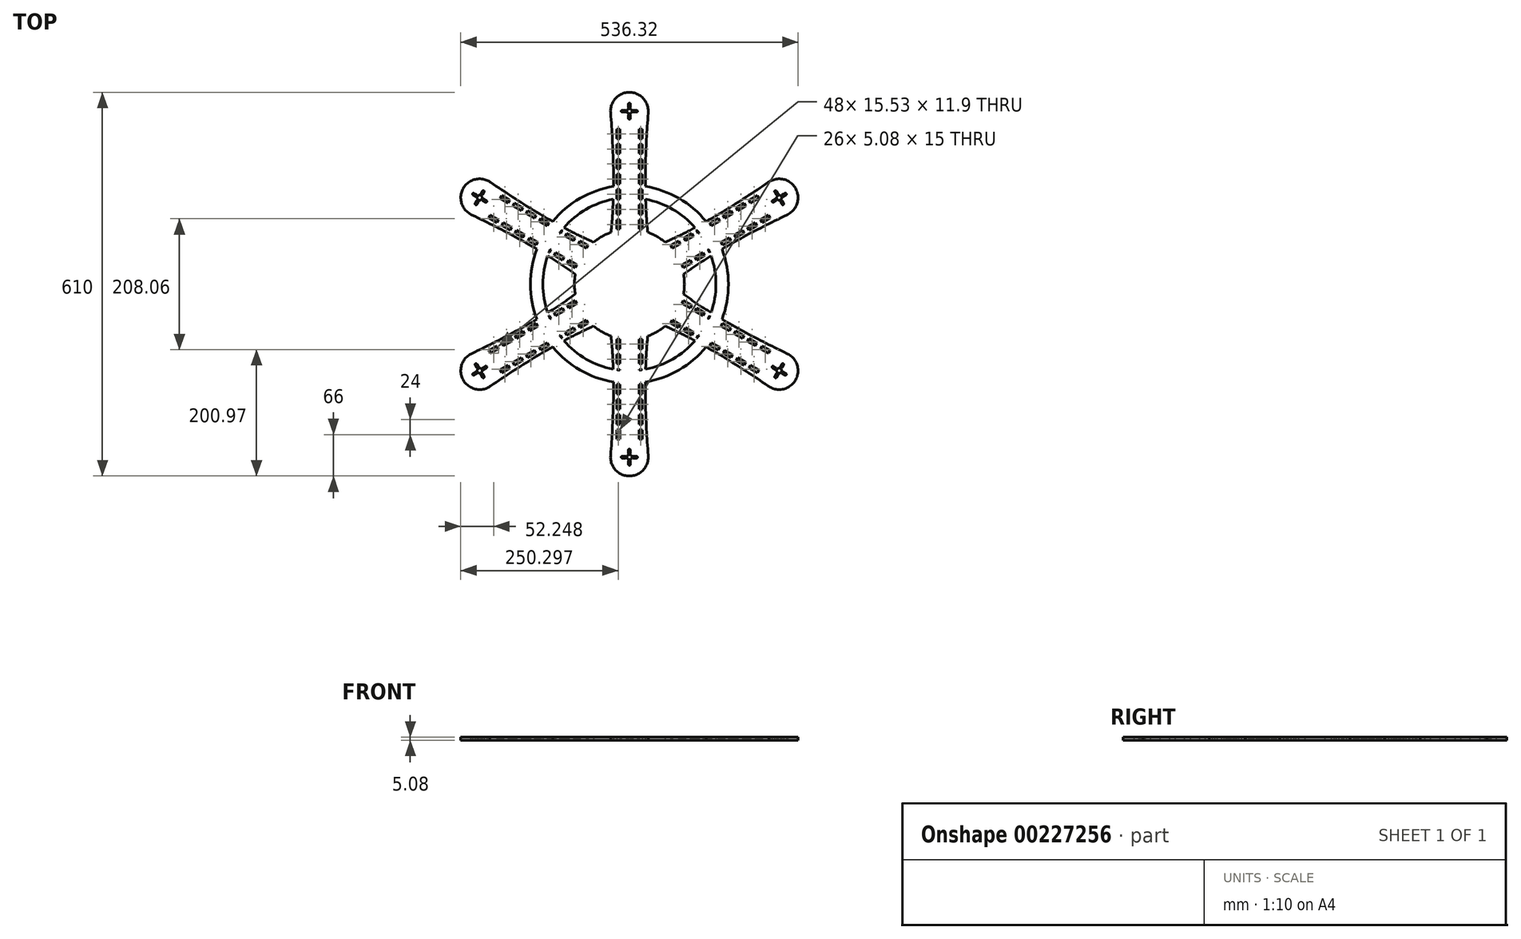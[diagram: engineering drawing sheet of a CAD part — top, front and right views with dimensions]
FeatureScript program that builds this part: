
annotation { "Feature Type Name" : "Feature", "Feature Type Description" : "" }
export const myFeature = defineFeature(function(context is Context, id is Id, definition is map)
    precondition{}
    {
        {
            var Q0;
            Q0=qCreatedBy(makeId("Top.planeOp"),FACE);
            var sketch = newSketch(context, id + "F0", { "sketchPlane" : qUnion([Q0])});
            skCircle(sketch, "E0", {"center": v(0, 0) * mm, "radius": 275 * mm, "construction": true});
            skCircle(sketch, "E1", {"center": v(0, 275) * mm, "radius": 30 * mm});
            skCircle(sketch, "E2", {"center": v(0, 0) * mm, "radius": 87.5 * mm});
            skCircle(sketch, "E3", {"center": v(0, 275) * mm, "radius": 4 * mm});
            skLineSegment(sketch, "E4", {"start": v(0, 275) * mm, "end": v(0, 281.5) * mm, "construction": true});
            skLineSegment(sketch, "E5", {"start": v(0, 281.5) * mm, "end": v(0, 286.5) * mm, "construction": true});
            skCircle(sketch, "E6", {"center": v(0, 286.5) * mm, "radius": 1.5 * mm});
            skCircle(sketch, "E7", {"center": v(0, 281.5) * mm, "radius": 1.5 * mm});
            skLineSegment(sketch, "E8", {"start": v(-1.5, 281.5) * mm, "end": v(-1.5, 286.5) * mm});
            skLineSegment(sketch, "E9.MirrorCS", {"start": v(1.5, 281.5) * mm, "end": v(1.5, 286.5) * mm});
            skLineSegment(sketch, "E10.1.0", {"start": v(-6.5, 276.5) * mm, "end": v(-11.5, 276.5) * mm});
            skCircle(sketch, "E10.1.1", {"center": v(-11.5, 275) * mm, "radius": 1.5 * mm});
            skLineSegment(sketch, "E10.1.2", {"start": v(-6.5, 273.5) * mm, "end": v(-11.5, 273.5) * mm});
            skCircle(sketch, "E10.1.3", {"center": v(-6.5, 275) * mm, "radius": 1.5 * mm});
            skLineSegment(sketch, "E10.2.0", {"start": v(-1.5, 268.5) * mm, "end": v(-1.5, 263.5) * mm});
            skCircle(sketch, "E10.2.1", {"center": v(0, 263.5) * mm, "radius": 1.5 * mm});
            skLineSegment(sketch, "E10.2.2", {"start": v(1.5, 268.5) * mm, "end": v(1.5, 263.5) * mm});
            skCircle(sketch, "E10.2.3", {"center": v(0, 268.5) * mm, "radius": 1.5 * mm});
            skLineSegment(sketch, "E10.3.0", {"start": v(6.5, 273.5) * mm, "end": v(11.5, 273.5) * mm});
            skCircle(sketch, "E10.3.1", {"center": v(11.5, 275) * mm, "radius": 1.5 * mm});
            skLineSegment(sketch, "E10.3.2", {"start": v(6.5, 276.5) * mm, "end": v(11.5, 276.5) * mm});
            skCircle(sketch, "E10.3.3", {"center": v(6.5, 275) * mm, "radius": 1.5 * mm});
            skFitSpline(sketch, "E11", {"points": [v(-29.96, 273.36) * mm, v(-29.27, 82.46) * mm], "startDerivative": vector(15.92, -208.81) * mm, "endDerivative": vector(-18.39, -172.18) * mm});
            skFitSpline(sketch, "E12.MirrorCS", {"points": [v(29.96, 273.36) * mm, v(29.27, 82.46) * mm], "startDerivative": vector(-15.92, -208.81) * mm, "endDerivative": vector(18.39, -172.18) * mm});
            skCircle(sketch, "E13", {"center": v(0, 0) * mm, "radius": 137.5 * mm});
            skCircle(sketch, "E14", {"center": v(0, 0) * mm, "radius": 157.5 * mm});
            skLineSegment(sketch, "E15.bottom", {"start": v(-20.4, 87.5) * mm, "end": v(-15.32, 87.5) * mm});
            skLineSegment(sketch, "E15.top", {"start": v(-20.4, 102.5) * mm, "end": v(-15.32, 102.5) * mm});
            skLineSegment(sketch, "E15.left", {"start": v(-20.4, 87.5) * mm, "end": v(-20.4, 102.5) * mm});
            skLineSegment(sketch, "E15.right", {"start": v(-15.32, 87.5) * mm, "end": v(-15.32, 102.5) * mm});
            skLineSegment(sketch, "E16.MirrorCS", {"start": v(15.32, 87.5) * mm, "end": v(15.32, 102.5) * mm});
            skLineSegment(sketch, "E17.MirrorCS", {"start": v(20.4, 102.5) * mm, "end": v(15.32, 102.5) * mm});
            skLineSegment(sketch, "E18.MirrorCS", {"start": v(20.4, 87.5) * mm, "end": v(20.4, 102.5) * mm});
            skLineSegment(sketch, "E19", {"start": v(15.32, 87.5) * mm, "end": v(20.4, 87.5) * mm});
            skLineSegment(sketch, "E20.0.1.0", {"start": v(-20.4, 111.5) * mm, "end": v(-20.4, 126.5) * mm});
            skLineSegment(sketch, "E20.0.1.1", {"start": v(-20.4, 126.5) * mm, "end": v(-15.32, 126.5) * mm});
            skLineSegment(sketch, "E20.0.1.2", {"start": v(-15.32, 111.5) * mm, "end": v(-15.32, 126.5) * mm});
            skLineSegment(sketch, "E20.0.1.3", {"start": v(-20.4, 111.5) * mm, "end": v(-15.32, 111.5) * mm});
            skLineSegment(sketch, "E20.0.1.4", {"start": v(15.32, 111.5) * mm, "end": v(15.32, 126.5) * mm});
            skLineSegment(sketch, "E20.0.1.5", {"start": v(20.4, 126.5) * mm, "end": v(15.32, 126.5) * mm});
            skLineSegment(sketch, "E20.0.1.6", {"start": v(20.4, 111.5) * mm, "end": v(20.4, 126.5) * mm});
            skLineSegment(sketch, "E20.0.1.7", {"start": v(15.32, 111.5) * mm, "end": v(20.4, 111.5) * mm});
            skLineSegment(sketch, "E20.0.2.0", {"start": v(-20.4, 135.5) * mm, "end": v(-20.4, 150.5) * mm});
            skLineSegment(sketch, "E20.0.2.1", {"start": v(-20.4, 150.5) * mm, "end": v(-15.32, 150.5) * mm});
            skLineSegment(sketch, "E20.0.2.2", {"start": v(-15.32, 135.5) * mm, "end": v(-15.32, 150.5) * mm});
            skLineSegment(sketch, "E20.0.2.3", {"start": v(-20.4, 135.5) * mm, "end": v(-15.32, 135.5) * mm});
            skLineSegment(sketch, "E20.0.2.4", {"start": v(15.32, 135.5) * mm, "end": v(15.32, 150.5) * mm});
            skLineSegment(sketch, "E20.0.2.5", {"start": v(20.4, 150.5) * mm, "end": v(15.32, 150.5) * mm});
            skLineSegment(sketch, "E20.0.2.6", {"start": v(20.4, 135.5) * mm, "end": v(20.4, 150.5) * mm});
            skLineSegment(sketch, "E20.0.2.7", {"start": v(15.32, 135.5) * mm, "end": v(20.4, 135.5) * mm});
            skLineSegment(sketch, "E20.0.3.0", {"start": v(-20.4, 159.5) * mm, "end": v(-20.4, 174.5) * mm});
            skLineSegment(sketch, "E20.0.3.1", {"start": v(-20.4, 174.5) * mm, "end": v(-15.32, 174.5) * mm});
            skLineSegment(sketch, "E20.0.3.2", {"start": v(-15.32, 159.5) * mm, "end": v(-15.32, 174.5) * mm});
            skLineSegment(sketch, "E20.0.3.3", {"start": v(-20.4, 159.5) * mm, "end": v(-15.32, 159.5) * mm});
            skLineSegment(sketch, "E20.0.3.4", {"start": v(15.32, 159.5) * mm, "end": v(15.32, 174.5) * mm});
            skLineSegment(sketch, "E20.0.3.5", {"start": v(20.4, 174.5) * mm, "end": v(15.32, 174.5) * mm});
            skLineSegment(sketch, "E20.0.3.6", {"start": v(20.4, 159.5) * mm, "end": v(20.4, 174.5) * mm});
            skLineSegment(sketch, "E20.0.3.7", {"start": v(15.32, 159.5) * mm, "end": v(20.4, 159.5) * mm});
            skLineSegment(sketch, "E20.0.4.0", {"start": v(-20.4, 183.5) * mm, "end": v(-20.4, 198.5) * mm});
            skLineSegment(sketch, "E20.0.4.1", {"start": v(-20.4, 198.5) * mm, "end": v(-15.32, 198.5) * mm});
            skLineSegment(sketch, "E20.0.4.2", {"start": v(-15.32, 183.5) * mm, "end": v(-15.32, 198.5) * mm});
            skLineSegment(sketch, "E20.0.4.3", {"start": v(-20.4, 183.5) * mm, "end": v(-15.32, 183.5) * mm});
            skLineSegment(sketch, "E20.0.4.4", {"start": v(15.32, 183.5) * mm, "end": v(15.32, 198.5) * mm});
            skLineSegment(sketch, "E20.0.4.5", {"start": v(20.4, 198.5) * mm, "end": v(15.32, 198.5) * mm});
            skLineSegment(sketch, "E20.0.4.6", {"start": v(20.4, 183.5) * mm, "end": v(20.4, 198.5) * mm});
            skLineSegment(sketch, "E20.0.4.7", {"start": v(15.32, 183.5) * mm, "end": v(20.4, 183.5) * mm});
            skLineSegment(sketch, "E20.0.5.0", {"start": v(-20.4, 207.5) * mm, "end": v(-20.4, 222.5) * mm});
            skLineSegment(sketch, "E20.0.5.1", {"start": v(-20.4, 222.5) * mm, "end": v(-15.32, 222.5) * mm});
            skLineSegment(sketch, "E20.0.5.2", {"start": v(-15.32, 207.5) * mm, "end": v(-15.32, 222.5) * mm});
            skLineSegment(sketch, "E20.0.5.3", {"start": v(-20.4, 207.5) * mm, "end": v(-15.32, 207.5) * mm});
            skLineSegment(sketch, "E20.0.5.4", {"start": v(15.32, 207.5) * mm, "end": v(15.32, 222.5) * mm});
            skLineSegment(sketch, "E20.0.5.5", {"start": v(20.4, 222.5) * mm, "end": v(15.32, 222.5) * mm});
            skLineSegment(sketch, "E20.0.5.6", {"start": v(20.4, 207.5) * mm, "end": v(20.4, 222.5) * mm});
            skLineSegment(sketch, "E20.0.5.7", {"start": v(15.32, 207.5) * mm, "end": v(20.4, 207.5) * mm});
            skLineSegment(sketch, "E20.0.6.0", {"start": v(-20.4, 231.5) * mm, "end": v(-20.4, 246.5) * mm});
            skLineSegment(sketch, "E20.0.6.1", {"start": v(-20.4, 246.5) * mm, "end": v(-15.32, 246.5) * mm});
            skLineSegment(sketch, "E20.0.6.2", {"start": v(-15.32, 231.5) * mm, "end": v(-15.32, 246.5) * mm});
            skLineSegment(sketch, "E20.0.6.3", {"start": v(-20.4, 231.5) * mm, "end": v(-15.32, 231.5) * mm});
            skLineSegment(sketch, "E20.0.6.4", {"start": v(15.32, 231.5) * mm, "end": v(15.32, 246.5) * mm});
            skLineSegment(sketch, "E20.0.6.5", {"start": v(20.4, 246.5) * mm, "end": v(15.32, 246.5) * mm});
            skLineSegment(sketch, "E20.0.6.6", {"start": v(20.4, 231.5) * mm, "end": v(20.4, 246.5) * mm});
            skLineSegment(sketch, "E20.0.6.7", {"start": v(15.32, 231.5) * mm, "end": v(20.4, 231.5) * mm});
            skLineSegment(sketch, "E20.direction1", {"start": v(-20.4, 87.5) * mm, "end": v(4.6, 87.5) * mm, "construction": true});
            skLineSegment(sketch, "E20.direction2", {"start": v(-20.4, 87.5) * mm, "end": v(-20.4, 111.5) * mm, "construction": true});
            skSolve(sketch);
        }
        {
            var Q0;
            Q0=makeQuery(id+"F0.imprint","IMPRINT",FACE,{"disambiguationData":[TD([[makeQuery(id+"F0.imprint","IMPRINT",EDGE,{"derivedFrom":sQuery(id+"F0.wireOp",EDGE,"E2")}),1.0]])]});
            var Q1;
            {var subQ7=sQuery(id+"F0.wireOp",EDGE,"E8");Q1=makeQuery(id+"F0.imprint","IMPRINT",FACE,{"disambiguationData":[TD([[makeQuery(id+"F0.imprint","IMPRINT",EDGE,{"derivedFrom":subQ7}),1.0]])]});}
            var Q2;
            {var subQ0=sQuery(id+"F0.wireOp",EDGE,"E1");var subQ1=sQuery(id+"F0.wireOp",EDGE,"E0");var subQ2=makeQuery(id+"F0.imprint","INTERSECT",VERTEX,{"disambiguationData":[OD(0.0)],"derivedFrom":[subQ1,subQ0]});Q2=makeQuery(id+"F0.imprint","IMPRINT",FACE,{"disambiguationData":[TD([[makeQuery(id+"F0.imprint","IMPRINT",EDGE,{"disambiguationData":[TD([[subQ2,-1.0]])],"derivedFrom":subQ1}),1.0]])]});}
            var Q3;
            {var subQ0=sQuery(id+"F0.wireOp",EDGE,"E11");var subQ1=sQuery(id+"F0.wireOp",EDGE,"E1");var subQ2=makeQuery(id+"F0.imprint","INTERSECT",VERTEX,{"disambiguationData":[OD(1.0)],"derivedFrom":[subQ1,subQ0]});Q3=makeQuery(id+"F0.imprint","IMPRINT",FACE,{"disambiguationData":[TD([[makeQuery(id+"F0.imprint","IMPRINT",EDGE,{"disambiguationData":[TD([[subQ2,-1.0]])],"derivedFrom":subQ1}),-1.0]])]});}
            var Q4;
            {var subQ0=sQuery(id+"F0.wireOp",EDGE,"E14");var subQ1=sQuery(id+"F0.wireOp",EDGE,"E11");var subQ2=makeQuery(id+"F0.imprint","INTERSECT",VERTEX,{"derivedFrom":[subQ1,subQ0]});Q4=makeQuery(id+"F0.imprint","IMPRINT",FACE,{"disambiguationData":[TD([[makeQuery(id+"F0.imprint","IMPRINT",EDGE,{"disambiguationData":[TD([[subQ2,-1.0]])],"derivedFrom":subQ1}),-1.0]])]});}
            var Q5;
            {var subQ0=sQuery(id+"F0.wireOp",EDGE,"E14");var subQ1=sQuery(id+"F0.wireOp",EDGE,"E11");var subQ2=makeQuery(id+"F0.imprint","INTERSECT",VERTEX,{"derivedFrom":[subQ1,subQ0]});Q5=makeQuery(id+"F0.imprint","IMPRINT",FACE,{"disambiguationData":[TD([[makeQuery(id+"F0.imprint","IMPRINT",EDGE,{"disambiguationData":[TD([[subQ2,-1.0]])],"derivedFrom":subQ1}),1.0]])]});}
            var Q6;
            {var subQ0=sQuery(id+"F0.wireOp",EDGE,"E11");var subQ1=sQuery(id+"F0.wireOp",EDGE,"E2");var subQ2=makeQuery(id+"F0.imprint","INTERSECT",VERTEX,{"derivedFrom":[subQ1,subQ0]});Q6=makeQuery(id+"F0.imprint","IMPRINT",FACE,{"disambiguationData":[TD([[makeQuery(id+"F0.imprint","IMPRINT",EDGE,{"disambiguationData":[TD([[subQ2,1.0]])],"derivedFrom":subQ1}),-1.0]])]});}
            extrude(context, id + "F1", {"entities" : qUnion([Q0, Q1, Q2, Q3, Q4, Q5, Q6]), "depth" : 5.08 * mm});
        }
        {
            var Q0;
            Q0=makeQuery(id+"F1.opExtrude","SWEPT_BODY",BODY,{"disambiguationData":[OSD([sQuery(id+"F0.wireOp",EDGE,"E1"),sQuery(id+"F0.wireOp",EDGE,"E2"),sQuery(id+"F0.wireOp",EDGE,"E3"),sQuery(id+"F0.wireOp",EDGE,"E6"),sQuery(id+"F0.wireOp",EDGE,"E7"),sQuery(id+"F0.wireOp",EDGE,"E8"),sQuery(id+"F0.wireOp",EDGE,"E9.MirrorCS"),sQuery(id+"F0.wireOp",EDGE,"E10.1.0"),sQuery(id+"F0.wireOp",EDGE,"E10.1.1"),sQuery(id+"F0.wireOp",EDGE,"E10.1.2"),sQuery(id+"F0.wireOp",EDGE,"E10.1.3"),sQuery(id+"F0.wireOp",EDGE,"E10.2.0"),sQuery(id+"F0.wireOp",EDGE,"E10.2.1"),sQuery(id+"F0.wireOp",EDGE,"E10.2.2"),sQuery(id+"F0.wireOp",EDGE,"E10.2.3"),sQuery(id+"F0.wireOp",EDGE,"E10.3.0"),sQuery(id+"F0.wireOp",EDGE,"E10.3.1"),sQuery(id+"F0.wireOp",EDGE,"E10.3.2"),sQuery(id+"F0.wireOp",EDGE,"E10.3.3"),sQuery(id+"F0.wireOp",EDGE,"E11"),sQuery(id+"F0.wireOp",EDGE,"E12.MirrorCS")])]});
            var Q1;
            Q1=makeQuery(id+"F1.opExtrude","SWEPT_FACE",FACE,{"disambiguationData":[OSD([sQuery(id+"F0.wireOp",EDGE,"E2")])]});
            circularPattern(context, id + "F2", {"operationType" : NewBodyOperationType.ADD, "entities" : qUnion([Q0]), "axis" : qUnion([Q1]), "angle" : 360 * degree, "instanceCount" : 6, "equalSpace" : true});
        }
        {
            var Q0;
            {var subQ5=sQuery(id+"F0.wireOp",EDGE,"E20.0.2.1");Q0=makeQuery(id+"F0.imprint","IMPRINT",FACE,{"disambiguationData":[TD([[makeQuery(id+"F0.imprint","IMPRINT",EDGE,{"derivedFrom":subQ5}),-1.0]])]});}
            var Q1;
            {var subQ5=sQuery(id+"F0.wireOp",EDGE,"E20.0.2.5");Q1=makeQuery(id+"F0.imprint","IMPRINT",FACE,{"disambiguationData":[TD([[makeQuery(id+"F0.imprint","IMPRINT",EDGE,{"derivedFrom":subQ5}),1.0]])]});}
            extrude(context, id + "F3", {"entities" : qUnion([Q0, Q1]), "operationType" : NewBodyOperationType.REMOVE, "depth" : 25 * mm});
        }
    });
